# Revit family: Doors-Overhead_Rapid-HöRMANN-SC1400_SEL_CoolMaster
name_source: partatom
category: Doors
revit_build: Autodesk Revit 2015 (Build: 20160512_1515(x64)
units: mm (PartAtom-declared; Revit-internal decimal feet)

## types (1)
- Doors-Overhead_Rapid-HöRMANN-SC1400_SEL_CoolMaster
    Acoustical Rating = STC 11
    Ambient Temperature = 40 °C
    Analytic Construction = <None>
    Application = Coolers/Interior Only
    Assembly Code = B2030410
    B = 0' - 3 29/32"
    Brochure URL = http://www.hormann-flexon.com
    CAD URL = http://www.hormann-flexon.com
    CSI Masterformat 2014 = 08 33 23.13 - Overhead Rapid Coiling Doors
    Country of Origin = United States of America
    Cut Sheet URL = Coming Soon
    Description = Overhead Coiling Doors
    Disconnect = 16 amp; Class K Fuse
    Emergency Opening = Operation via Chain Hoist
    Enclosure Protection Category Control Box = NEMA 4, UL/cUL Listed
    Enclosure Protection Category Motor = NEMA 3
    Fire Rating = Non-Rated, Non-Conforming Exit
    Freight Class = 70
    Full Load Amps = 13 A
    Guide Track Design = Low Profile - Standard
    Hardware Set = Hardware is Manufacturer furnished.
    Heat Transfer Coefficient (U) = 0.73 BTU/(h·ft²·°F)
    Horse Power = 2 hp
    Installation Manual URL = http://www.hormann-flexon.com
    Insulation Class - ICL = F
    LEED Credit = MR Credit 2; MR Credit 4; EQ Credit 5
    Manufacturer = Hörmann Flexon, LLC.
    Manufacturer Disclaimer = We believe this information to be the best currently available, and is offered only as a possible suggestion and guideline in design exploration you may undertake. It is subject to revision without notice. We make no guarantee of results and assume no obligation or liability whatsoever in connection with this information. Confirm all information with the Manufacturer prior to implementation.
    Manufacturer Location = Starpointe Business Park, 117 Starpointe Blvd. Burgettstown, PA 15021-9506
    Model = Speed-Commander® 1400 SEL Cool Master
    Motor Frequency = 60 Hz
    Mounting Diagram URL = Coming Soon
    Operating Speed = Up to 80 in per second opening, and 30 in per second closing
    Operator_Motor = GfA Elektromaten - F18
    PDF URL = http://www.hormann-flexon.com
    Panel Solid P2 = Panel Fabric Master : P2
    Panel Solid P3 = Panel Fabric Master : P3
    Panel Win P2 = Panel Fabric Master Win : P2
    Panel Win P3 = Panel Fabric Master Win : P3
    Power Rating = 2 hp
    Product Options = Stainless Steel Components, Battery Pack
    Publish Date = October 7, 2016
    RPM = 1730
    Representative Disclaimer = Hörmann Flexon products are sold and installed through a nationwide independent network of distributors.
    Roll Tube Diameter = 0' - 6"
    Service Factor = 2 SF
    Size Range = Up to 14'-0" wide by 16'-0" high
    Sizing Disclaimer = Openings up to fourteen feet wide by sixteen feet high are standard construction. Please consult Hörmann Flexon for larger sizes.
    Solar Heat Gain Coefficient = 0.81
    Specifications URL = http://www.hormann-flexon.com
    Standard Power Requirement = 132V 3PH, 60 Hz
    Thermal Resistance (R) = 1.3700 (h·ft²·°F)/BTU
    Thickness = 0' - 0 1/8"
    Type Comments = Energy-saving high performance door ideal for cooler applictions.
    URL = http://www.hormann-flexon.com
    UV Resistance = -
    Version Number = v. 001
    Visual Light Transmittance = 0.83
    Wall Closure = By host
    Warranty = 5 & 2 Limited Warranty: The motor (excluding catch) and panel material are guarranteed against defects in materials and workmanship for a period of 5 years. All other mechanical and electrical components are warranted against defects for a period of 2 full years.
    Wind Load Resistance = 0.46 psf / 15 mph
    ifcName = ifcDoor

## geometry (parser evidence)
native form markers: Extrusion x1, Sweep x52
no freeform markers — native parametric forms only
